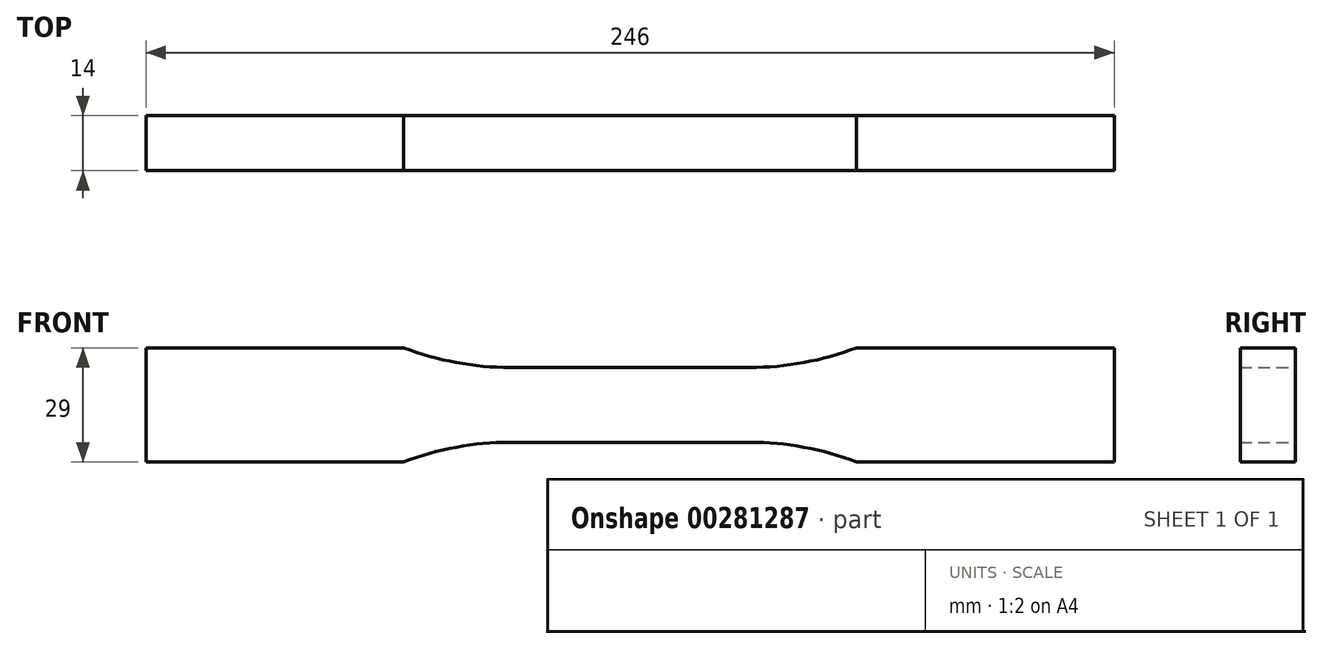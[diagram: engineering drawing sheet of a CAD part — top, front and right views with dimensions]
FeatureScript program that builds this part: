
annotation { "Feature Type Name" : "Feature", "Feature Type Description" : "" }
export const myFeature = defineFeature(function(context is Context, id is Id, definition is map)
    precondition{}
    {
        {
            var Q0;
            Q0=qCreatedBy(makeId("Front.planeOp"),FACE);
            var sketch = newSketch(context, id + "F0", { "sketchPlane" : qUnion([Q0])});
            skLineSegment(sketch, "E0", {"start": v(0, 9.5) * mm, "end": v(30.39, 9.5) * mm});
            skArc(sketch, "E1", {"start": v(30.39, 9.5) * mm, "mid": v(44.17, 10.76) * mm, "end": v(57.5, 14.5) * mm});
            skLineSegment(sketch, "E2", {"start": v(57.5, 14.5) * mm, "end": v(123, 14.5) * mm});
            skLineSegment(sketch, "E3", {"start": v(123, 14.5) * mm, "end": v(123, 0) * mm});
            skLineSegment(sketch, "E4.MirrorCS", {"start": v(0, -9.5) * mm, "end": v(30.39, -9.5) * mm});
            skLineSegment(sketch, "E5.MirrorCS", {"start": v(123, -14.5) * mm, "end": v(123, 0) * mm});
            skLineSegment(sketch, "E6.MirrorCS", {"start": v(57.5, -14.5) * mm, "end": v(123, -14.5) * mm});
            skArc(sketch, "E7.MirrorCS", {"start": v(30.39, -9.5) * mm, "mid": v(44.17, -10.76) * mm, "end": v(57.5, -14.5) * mm});
            skArc(sketch, "E8.MirrorCS", {"start": v(-30.39, -9.5) * mm, "mid": v(-44.17, -10.76) * mm, "end": v(-57.5, -14.5) * mm});
            skLineSegment(sketch, "E9.MirrorCS", {"start": v(-57.5, -14.5) * mm, "end": v(-123, -14.5) * mm});
            skLineSegment(sketch, "E10.MirrorCS", {"start": v(0, 9.5) * mm, "end": v(-30.39, 9.5) * mm});
            skArc(sketch, "E11.MirrorCS", {"start": v(-30.39, 9.5) * mm, "mid": v(-44.17, 10.76) * mm, "end": v(-57.5, 14.5) * mm});
            skLineSegment(sketch, "E12.MirrorCS", {"start": v(-57.5, 14.5) * mm, "end": v(-123, 14.5) * mm});
            skLineSegment(sketch, "E13.MirrorCS", {"start": v(-123, -14.5) * mm, "end": v(-123, 0) * mm});
            skLineSegment(sketch, "E14.MirrorCS", {"start": v(-123, 14.5) * mm, "end": v(-123, 0) * mm});
            skLineSegment(sketch, "E15.MirrorCS", {"start": v(0, -9.5) * mm, "end": v(-30.39, -9.5) * mm});
            skSolve(sketch);
        }
        {
            var Q0;
            Q0=makeQuery(id+"F0.imprint","IMPRINT",FACE,{"disambiguationData":[TD([[makeQuery(id+"F0.imprint","IMPRINT",EDGE,{"derivedFrom":sQuery(id+"F0.wireOp",EDGE,"E1")}),-1.0]])]});
            extrude(context, id + "F1", {"entities" : qUnion([Q0]), "endBound" : BoundingType.SYMMETRIC, "depth" : 14 * mm});
        }
    });
